# Revit family: WC AUSTRAL_RFA
name_source: partatom
category: Aparatos sanitarios
units: mm (PartAtom-declared; Revit-internal decimal feet)

## family parameters
Compartido = No
Corte con vacíos al cargar = No
Cota de conector redondo = Diámetro de uso
Número OmniClass = 23.45.00.00
Punto de cálculo de habitación = No
Se basa en plano de trabajo = No
Siempre vertical = Sí
Tipo de pieza = Normal
Título OmniClass = Sanitary, Laundry, and Cleaning Equipment

## types (1)
- WC AUSTRAL
    Comentarios de tipo = Ceramic
    Data Sheet = https://www.helvex.com.mx
    Descripción = Diseño ergonómico de construcción robusta
con cerámica de 10mm de espesor, con
sistema de descarga Turvex con sifón jet
y espejo de agua óptimo, mueble libre de
alabeo (base plana).
    Elevación por defecto = 0"
    Fabricante = HELVEX
    High Gloss Ceramic = High Gloss Ceramic
    Imagen de tipo = product719.jpg
    Inlet Threads = Feeding: Ø15/16" - 14 NS - 1;  Flush: Couple With Sanitary Flange
    Instructive = https://www.helvex.com.mx
    Max. Working Pressure = 85.3 psi
    Maximum Consumption = 1.0 gpf
    Min. Working Pressure = 3.6 psi
    Modelo = WC AUSTRAL
    Total Height = 31"
    Total Length = 27"
    Total Width = 16"
    URL = https://www.helvex.com.mx

## geometry (parser evidence)
native form markers: Sweep x3
no freeform markers — native parametric forms only
